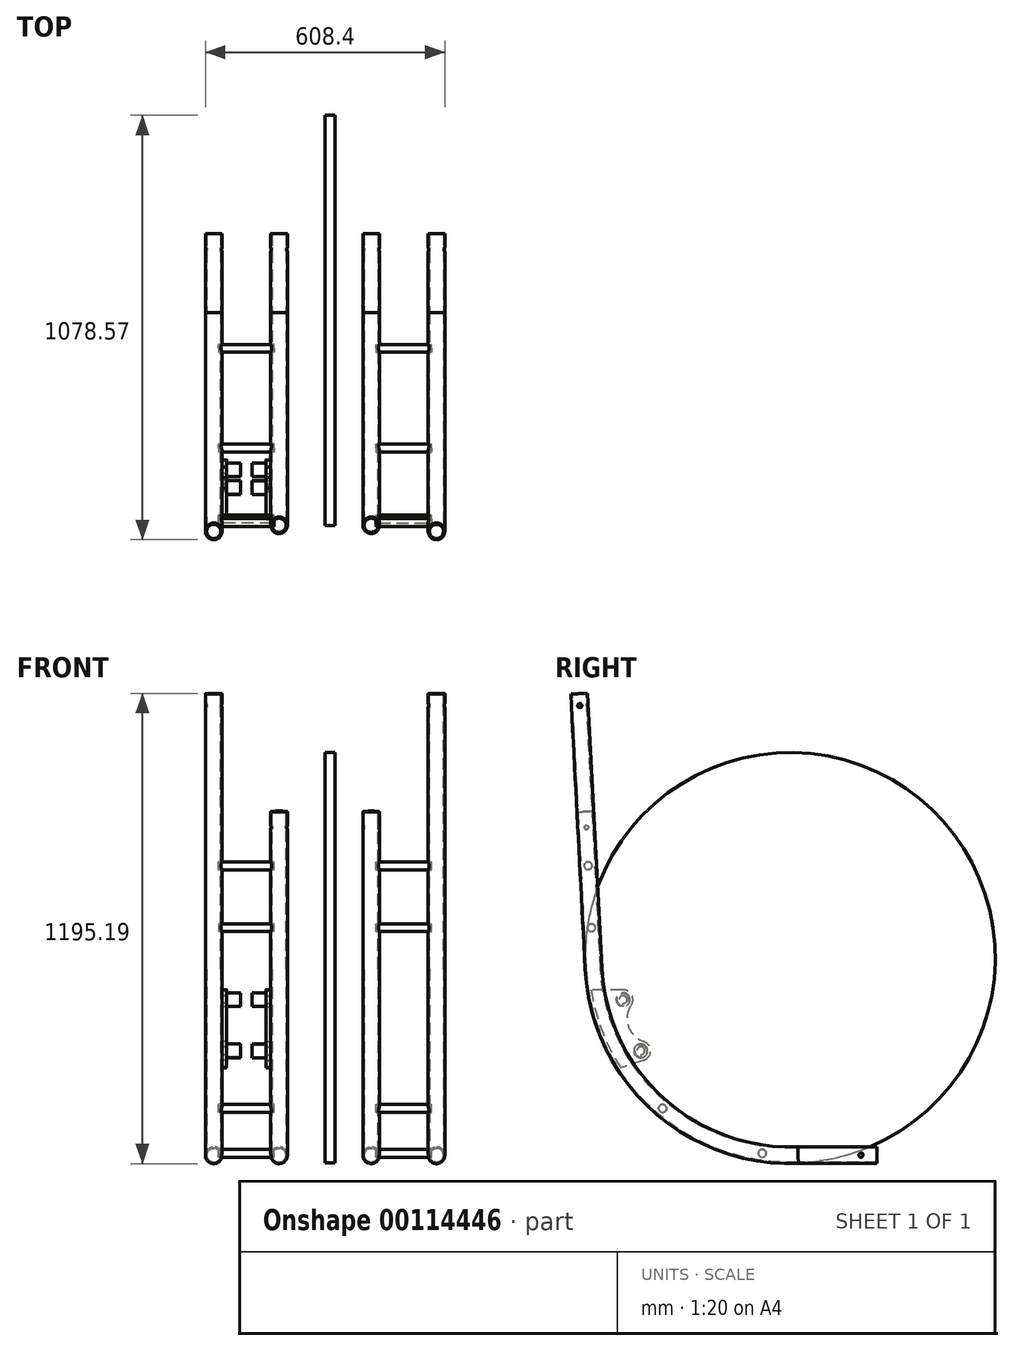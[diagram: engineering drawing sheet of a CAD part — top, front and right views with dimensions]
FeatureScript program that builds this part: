
annotation { "Feature Type Name" : "Feature", "Feature Type Description" : "" }
export const myFeature = defineFeature(function(context is Context, id is Id, definition is map)
    precondition{}
    {
        {
            var Q0;
            Q0=qCreatedBy(makeId("Right.planeOp"),FACE);
            var sketch = newSketch(context, id + "F0", { "sketchPlane" : qUnion([Q0])});
            skArc(sketch, "E0", {"start": v(-719.7, 473.42) * mm, "mid": v(-557.1, 129.96) * mm, "end": v(-200, 0) * mm});
            skLineSegment(sketch, "E1", {"start": v(-719.7, 473.42) * mm, "end": v(-756.33, 1172.46) * mm});
            skLineSegment(sketch, "E2", {"start": v(-200, 0) * mm, "end": v(0, 0) * mm});
            skSolve(sketch);
        }
        {
            var Q0;
            Q0=qCreatedBy(makeId("Front.planeOp"),FACE);
            var sketch = newSketch(context, id + "F1", { "sketchPlane" : qUnion([Q0])});
            skCircle(sketch, "E3", {"center": v(0, 0) * mm, "radius": 21.2 * mm});
            skCircle(sketch, "E4.0", {"center": v(0, 0) * mm, "radius": 17.95 * mm});
            skSolve(sketch);
        }
        {
            var Q0;
            Q0=makeQuery(id+"F1.imprint","IMPRINT",FACE,{"disambiguationData":[TD([[makeQuery(id+"F1.imprint","IMPRINT",EDGE,{"derivedFrom":sQuery(id+"F1.wireOp",EDGE,"E3")}),1.0]])]});
            var Q1;
            Q1 = qBodyType(qCreatedBy(id + "F0" ,EDGE), BodyType.WIRE);
            sweep(context, id + "F2", {"profiles" : qUnion([Q0]), "path" : qUnion([Q1])});
        }
        {
            var Q0;
            Q0=qCreatedBy(makeId("Right.planeOp"),FACE);
            cPlane(context, id + "F3", {"entities" : qUnion([Q0]), "cplaneType" : CPlaneType.OFFSET, "offset" : 166 * mm, "width" : 150 * mm, "height" : 150 * mm});
        }
        {
            var Q0;
            Q0=qCreatedBy(id+"F3.planeOp",FACE);
            var sketch = newSketch(context, id + "F4", { "sketchPlane" : qUnion([Q0])});
            skArc(sketch, "E5", {"start": v(-719.7, 473.42) * mm, "mid": v(-557.1, 129.96) * mm, "end": v(-200, 0) * mm});
            skLineSegment(sketch, "E6", {"start": v(-719.7, 473.42) * mm, "end": v(-740.63, 872.87) * mm});
            skLineSegment(sketch, "E7", {"start": v(-200, 0) * mm, "end": v(0, 0) * mm});
            skSolve(sketch);
        }
        {
            var Q0;
            Q0 = qSketchRegion(id + "F1", true);
            var sketch = newSketch(context, id + "F5", { "sketchPlane" : qUnion([Q0])});
            skCircle(sketch, "E8", {"center": v(166, 0) * mm, "radius": 21.2 * mm});
            skCircle(sketch, "E9.0", {"center": v(166, 0) * mm, "radius": 17.95 * mm});
            skSolve(sketch);
        }
        {
            var Q0;
            Q0=makeQuery(id+"F5.imprint","IMPRINT",FACE,{"disambiguationData":[TD([[makeQuery(id+"F5.imprint","IMPRINT",EDGE,{"derivedFrom":sQuery(id+"F5.wireOp",EDGE,"E8")}),1.0]])]});
            var Q1;
            Q1 = qBodyType(qCreatedBy(id + "F4" ,EDGE), BodyType.WIRE);
            sweep(context, id + "F6", {"operationType" : NewBodyOperationType.ADD, "profiles" : qUnion([Q0]), "path" : qUnion([Q1])});
        }
        {
            var Q0;
            Q0=qCreatedBy(makeId("Right.planeOp"),FACE);
            cPlane(context, id + "F7", {"entities" : qUnion([Q0]), "cplaneType" : CPlaneType.OFFSET, "offset" : 83 * mm, "width" : 150 * mm, "height" : 150 * mm});
        }
        {
            var Q0;
            Q0=qCreatedBy(id+"F7.planeOp",FACE);
            var sketch = newSketch(context, id + "F8", { "sketchPlane" : qUnion([Q0])});
            skCircle(sketch, "E10", {"center": v(-40, 0) * mm, "radius": 5.25 * mm});
            skCircle(sketch, "E11", {"center": v(-754.76, 1142.36) * mm, "radius": 5.25 * mm});
            skSolve(sketch);
        }
        {
            var Q0;
            Q0=makeQuery(id+"F8.imprint","IMPRINT",FACE,{"disambiguationData":[TD([[makeQuery(id+"F8.imprint","IMPRINT",EDGE,{"derivedFrom":sQuery(id+"F8.wireOp",EDGE,"E11")}),1.0]])]});
            var Q1;
            Q1=makeQuery(id+"F8.imprint","IMPRINT",FACE,{"disambiguationData":[TD([[makeQuery(id+"F8.imprint","IMPRINT",EDGE,{"derivedFrom":sQuery(id+"F8.wireOp",EDGE,"E10")}),1.0]])]});
            extrude(context, id + "F9", {"entities" : qUnion([Q0, Q1]), "operationType" : NewBodyOperationType.REMOVE, "endBound" : BoundingType.THROUGH_ALL, "oppositeDirection" : true, "depth" : 100 * mm, "hasSecondDirection" : true, "secondDirectionBound" : SecondDirectionBoundingType.THROUGH_ALL, "secondDirectionOppositeDirection" : false, "secondDirectionDepth" : 25 * mm});
        }
        {
            var Q0;
            Q0=qCreatedBy(id+"F7.planeOp",FACE);
            var sketch = newSketch(context, id + "F10", { "sketchPlane" : qUnion([Q0])});
            skCircle(sketch, "E12", {"center": v(-737.57, 832.97) * mm, "radius": 5.25 * mm});
            skSolve(sketch);
        }
        {
            var Q0;
            Q0=makeQuery(id+"F10.imprint","IMPRINT",FACE,{"disambiguationData":[TD([[makeQuery(id+"F10.imprint","IMPRINT",EDGE,{"derivedFrom":sQuery(id+"F10.wireOp",EDGE,"E12")}),1.0]])]});
            extrude(context, id + "F11", {"entities" : qUnion([Q0]), "operationType" : NewBodyOperationType.REMOVE, "endBound" : BoundingType.THROUGH_ALL, "depth" : 100 * mm});
        }
        {
            var Q0;
            Q0=qCreatedBy(id+"F3.planeOp",FACE);
            cPlane(context, id + "F12", {"entities" : qUnion([Q0]), "cplaneType" : CPlaneType.OFFSET, "offset" : 21 * mm, "oppositeDirection" : true, "width" : 150 * mm, "height" : 150 * mm});
        }
        {
            var Q0;
            Q0=qCreatedBy(id+"F12.planeOp",FACE);
            var sketch = newSketch(context, id + "F13", { "sketchPlane" : qUnion([Q0])});
            skLineSegment(sketch, "E13", {"start": v(-690.74, 330) * mm, "end": v(-690.74, 0) * mm});
            skCircle(sketch, "E14", {"center": v(-644.68, 395) * mm, "radius": 10 * mm});
            skCircle(sketch, "E15", {"center": v(-599.68, 265) * mm, "radius": 10 * mm});
            skArc(sketch, "E16", {"start": v(-627.35, 376.98) * mm, "mid": v(-621.84, 405.17) * mm, "end": v(-646.48, 419.93) * mm});
            skArc(sketch, "E17", {"start": v(-592.84, 240.95) * mm, "mid": v(-574.68, 264.98) * mm, "end": v(-592.8, 289.03) * mm});
            skLineSegment(sketch, "E18", {"start": v(-646.48, 419.93) * mm, "end": v(-714, 419.93) * mm});
            skLineSegment(sketch, "E19", {"start": v(-592.84, 240.95) * mm, "end": v(-638.53, 225.46) * mm});
            skArc(sketch, "E20", {"start": v(-627.35, 376.98) * mm, "mid": v(-630.33, 325.05) * mm, "end": v(-592.8, 289.03) * mm});
            skArc(sketch, "E21.0", {"start": v(-726.14, 419.93) * mm, "mid": v(-698.65, 316.82) * mm, "end": v(-650.37, 221.65) * mm});
            skLineSegment(sketch, "E22", {"start": v(-714, 419.93) * mm, "end": v(-726.14, 419.93) * mm});
            skLineSegment(sketch, "E23", {"start": v(-638.53, 225.46) * mm, "end": v(-650.37, 221.65) * mm});
            skPoint(sketch, "E24.trimOffspring.end.orphan", {"position": v(-200, 0) * mm});
            skPoint(sketch, "E25.0.start.orphan", {"position": v(-719.7, 473.42) * mm});
            skSolve(sketch);
        }
        {
            var Q0;
            Q0=makeQuery(id+"F13.imprint","IMPRINT",FACE,{"disambiguationData":[TD([[makeQuery(id+"F13.imprint","IMPRINT",EDGE,{"derivedFrom":sQuery(id+"F13.wireOp",EDGE,"E14")}),-1.0]])]});
            extrude(context, id + "F14", {"entities" : qUnion([Q0]), "oppositeDirection" : true, "depth" : 12 * mm});
        }
        {
            var Q0;
            Q0=makeQuery(id+"F14.opExtrude","CAP_FACE",FACE,{"disambiguationData":[OSD([sQuery(id+"F13.wireOp",EDGE,"E25.0"),sQuery(id+"F13.wireOp",EDGE,"E14"),sQuery(id+"F13.wireOp",EDGE,"E15"),sQuery(id+"F13.wireOp",EDGE,"E16"),sQuery(id+"F13.wireOp",EDGE,"E17"),sQuery(id+"F13.wireOp",EDGE,"E18"),sQuery(id+"F13.wireOp",EDGE,"E19"),sQuery(id+"F13.wireOp",EDGE,"E20")])],"isStart":false});
            var sketch = newSketch(context, id + "F15", { "sketchPlane" : qUnion([Q0])});
            skCircle(sketch, "E26", {"center": v(644.68, 395) * mm, "radius": 17.5 * mm});
            skCircle(sketch, "E27.0", {"center": v(644.68, 395) * mm, "radius": 15.5 * mm});
            skCircle(sketch, "E28", {"center": v(599.68, 265) * mm, "radius": 17.5 * mm});
            skCircle(sketch, "E29.0", {"center": v(599.68, 265) * mm, "radius": 15.5 * mm});
            skSolve(sketch);
        }
        {
            var Q0;
            Q0=makeQuery(id+"F15.imprint","IMPRINT",FACE,{"disambiguationData":[TD([[makeQuery(id+"F15.imprint","IMPRINT",EDGE,{"derivedFrom":sQuery(id+"F15.wireOp",EDGE,"E26")}),1.0]])]});
            var Q1;
            Q1=makeQuery(id+"F15.imprint","IMPRINT",FACE,{"disambiguationData":[TD([[makeQuery(id+"F15.imprint","IMPRINT",EDGE,{"derivedFrom":sQuery(id+"F15.wireOp",EDGE,"E28")}),1.0]])]});
            extrude(context, id + "F16", {"entities" : qUnion([Q0, Q1]), "operationType" : NewBodyOperationType.ADD, "depth" : 35 * mm});
        }
        {
            var Q0;
            Q0=makeQuery(id+"F14.opExtrude","SWEPT_BODY",BODY,{"disambiguationData":[OSD([sQuery(id+"F13.wireOp",EDGE,"E25.0"),sQuery(id+"F13.wireOp",EDGE,"E14"),sQuery(id+"F13.wireOp",EDGE,"E15"),sQuery(id+"F13.wireOp",EDGE,"E16"),sQuery(id+"F13.wireOp",EDGE,"E17"),sQuery(id+"F13.wireOp",EDGE,"E18"),sQuery(id+"F13.wireOp",EDGE,"E19"),sQuery(id+"F13.wireOp",EDGE,"E20")])]});
            var Q1;
            Q1=qCreatedBy(id+"F7.planeOp",FACE);
            mirror(context, id + "F17", {"entities" : qUnion([Q0]), "mirrorPlane" : qUnion([Q1])});
        }
        {
            var Q0;
            Q0=qCreatedBy(id+"F7.planeOp",FACE);
            var sketch = newSketch(context, id + "F18", { "sketchPlane" : qUnion([Q0])});
            skCircle(sketch, "E30", {"center": v(-291.13, 4.62) * mm, "radius": 10 * mm});
            skCircle(sketch, "E31", {"center": v(-544.36, 118.75) * mm, "radius": 10 * mm});
            skCircle(sketch, "E32", {"center": v(-725.17, 577.89) * mm, "radius": 10 * mm});
            skCircle(sketch, "E33", {"center": v(-733.42, 735.28) * mm, "radius": 10 * mm});
            skSolve(sketch);
        }
        {
            var Q0;
            Q0 = qSketchRegion(id + "F18", true);
            extrude(context, id + "F19", {"entities" : qUnion([Q0]), "operationType" : NewBodyOperationType.ADD, "endBound" : BoundingType.SYMMETRIC, "depth" : 140 * mm});
        }
        {
            var Q0;
            Q0=qCreatedBy(id+"F7.planeOp",FACE);
            cPlane(context, id + "F20", {"entities" : qUnion([Q0]), "cplaneType" : CPlaneType.OFFSET, "offset" : 200 * mm, "width" : 150 * mm, "height" : 150 * mm});
        }
        {
            var Q0;
            Q0=makeQuery(id+"F2.opSweep","SWEPT_BODY",BODY,{"disambiguationData":[OSD([sQuery(id+"F0.wireOp",EDGE,"E1"),sQuery(id+"F1.wireOp",EDGE,"E3"),sQuery(id+"F1.wireOp",EDGE,"E4.0")])]});
            var Q1;
            Q1=qCreatedBy(id+"F20.planeOp",FACE);
            mirror(context, id + "F21", {"entities" : qUnion([Q0]), "mirrorPlane" : qUnion([Q1])});
        }
        {
            var Q0;
            Q0=qCreatedBy(id+"F20.planeOp",FACE);
            var sketch = newSketch(context, id + "F22", { "sketchPlane" : qUnion([Q0])});
            skCircle(sketch, "E34", {"center": v(-220.13, 501.63) * mm, "radius": 521.2 * mm});
            skSolve(sketch);
        }
        {
            var Q0;
            Q0=makeQuery(id+"F22.imprint","IMPRINT",FACE,{"disambiguationData":[TD([[makeQuery(id+"F22.imprint","IMPRINT",EDGE,{"derivedFrom":sQuery(id+"F22.wireOp",EDGE,"E34")}),1.0]])]});
            extrude(context, id + "F23", {"entities" : qUnion([Q0]), "depth" : 25 * mm});
        }
    });
